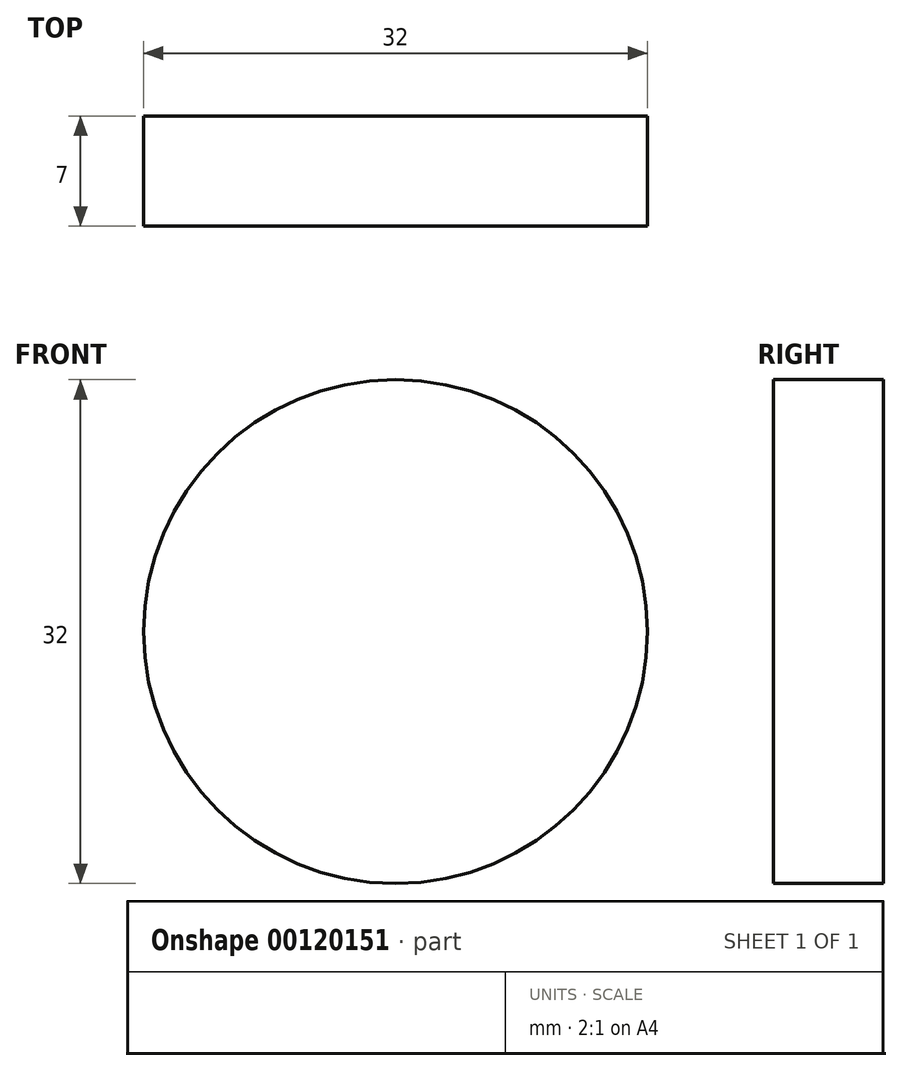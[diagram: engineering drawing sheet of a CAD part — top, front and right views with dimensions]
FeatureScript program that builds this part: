
annotation { "Feature Type Name" : "Feature", "Feature Type Description" : "" }
export const myFeature = defineFeature(function(context is Context, id is Id, definition is map)
    precondition{}
    {
        {
            var Q0;
            Q0=qCreatedBy(makeId("Front.planeOp"),FACE);
            var sketch = newSketch(context, id + "F0", { "sketchPlane" : qUnion([Q0])});
            skCircle(sketch, "E0", {"center": v(0, 0) * mm, "radius": 16 * mm});
            skSolve(sketch);
        }
        {
            var Q0;
            Q0 = qSketchRegion(id + "F0", true);
            extrude(context, id + "F1", {"entities" : qUnion([Q0]), "depth" : 7 * mm});
        }
    });
